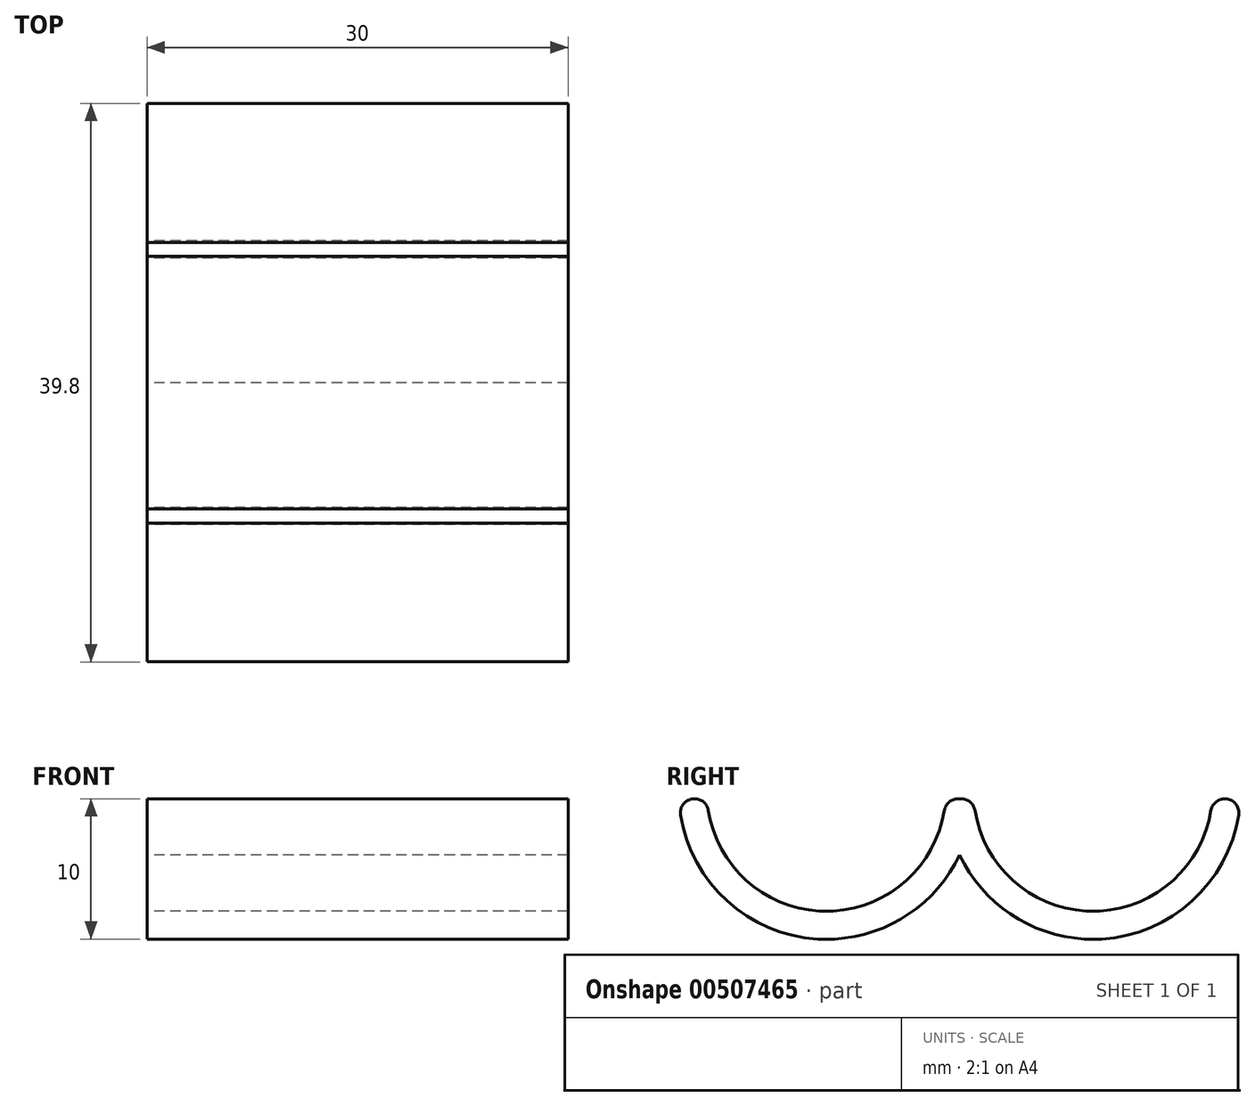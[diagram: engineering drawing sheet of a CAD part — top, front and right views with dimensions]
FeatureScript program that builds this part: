
annotation { "Feature Type Name" : "Feature", "Feature Type Description" : "" }
export const myFeature = defineFeature(function(context is Context, id is Id, definition is map)
    precondition{}
    {
        {
            var Q0;
            Q0=qCreatedBy(makeId("Right.planeOp"),FACE);
            var sketch = newSketch(context, id + "F0", { "sketchPlane" : qUnion([Q0])});
            skLineSegment(sketch, "E0", {"start": v(0, 0) * mm, "end": v(-1, 0) * mm});
            skLineSegment(sketch, "E1", {"start": v(-1, 0) * mm, "end": v(-1, 4) * mm});
            skLineSegment(sketch, "E2", {"start": v(-1, 8) * mm, "end": v(-2, 8) * mm});
            skPoint(sketch, "E3", {"position": v(-11, 0) * mm});
            skArc(sketch, "E4", {"start": v(-19, 8) * mm, "mid": v(-16.52, 2.48) * mm, "end": v(-11, 0) * mm});
            skLineSegment(sketch, "E5.MirrorCS", {"start": v(19, 8) * mm, "end": v(17, 8) * mm});
            skLineSegment(sketch, "E6.MirrorCS", {"start": v(-1, 8) * mm, "end": v(0, 8) * mm});
            skArc(sketch, "E7.MirrorCS", {"start": v(17, 8) * mm, "mid": v(14.52, 2.48) * mm, "end": v(9, 0) * mm});
            skPoint(sketch, "E8.MirrorP", {"position": v(9, 0) * mm});
            skArc(sketch, "E9.trimOffspring", {"start": v(-10, 0) * mm, "mid": v(-4.48, 2.48) * mm, "end": v(-2, 8) * mm});
            skArc(sketch, "E10.trimOffspring", {"start": v(8, 0) * mm, "mid": v(2.48, 2.48) * mm, "end": v(0, 8) * mm});
            skArc(sketch, "E11.0", {"start": v(-21, 7.88) * mm, "mid": v(-17.94, 1.06) * mm, "end": v(-11.12, -2) * mm});
            skArc(sketch, "E12.0", {"start": v(-9.88, -2) * mm, "mid": v(-4.62, -0.22) * mm, "end": v(-1, 4) * mm});
            skArc(sketch, "E13.0", {"start": v(7.88, -2) * mm, "mid": v(2.62, -0.22) * mm, "end": v(-1, 4) * mm});
            skArc(sketch, "E14.0", {"start": v(19, 7.88) * mm, "mid": v(15.94, 1.06) * mm, "end": v(9.12, -2) * mm});
            skLineSegment(sketch, "E15", {"start": v(-11.12, -2) * mm, "end": v(-9.88, -2) * mm});
            skLineSegment(sketch, "E16", {"start": v(7.88, -2) * mm, "end": v(9.12, -2) * mm});
            skLineSegment(sketch, "E17.trimOffspring", {"start": v(-10, 0) * mm, "end": v(-11, 0) * mm});
            skPoint(sketch, "E18.start.orphan", {"position": v(-22, 8) * mm});
            skLineSegment(sketch, "E19", {"start": v(-19, 8) * mm, "end": v(-21, 8) * mm});
            skLineSegment(sketch, "E20", {"start": v(-21, 7.88) * mm, "end": v(-21, 8) * mm});
            skPoint(sketch, "E21.end.orphan", {"position": v(-22, 0) * mm});
            skPoint(sketch, "E22.orphan", {"position": v(-19, 0) * mm});
            skLineSegment(sketch, "E23", {"start": v(19, 7.88) * mm, "end": v(19, 8) * mm});
            skPoint(sketch, "E24.MirrorCS.end.orphan", {"position": v(20, 8) * mm});
            skPoint(sketch, "E25.MirrorCS.end.orphan", {"position": v(20, 0) * mm});
            skPoint(sketch, "E26.orphan", {"position": v(17, 0) * mm});
            skLineSegment(sketch, "E27.trimOffspring", {"start": v(8, 0) * mm, "end": v(9, 0) * mm});
            skPoint(sketch, "E28.MirrorCS.start.orphan", {"position": v(-1, 0) * mm});
            skSolve(sketch);
        }
        {
            var Q0;
            Q0=makeQuery(id+"F0.imprint","IMPRINT",FACE,{"disambiguationData":[TD([[makeQuery(id+"F0.imprint","IMPRINT",EDGE,{"derivedFrom":sQuery(id+"F0.wireOp",EDGE,"E2")}),1.0]])]});
            extrude(context, id + "F1", {"entities" : qUnion([Q0]), "depth" : 30 * mm});
        }
        {
            var Q0;
            Q0=makeQuery(id+"F1.opExtrude","SWEPT_EDGE",EDGE,{"disambiguationData":[OSD([sQuery(id+"F0.wireOp",EDGE,"E4"),sQuery(id+"F0.wireOp",EDGE,"E19")])]});
            fillet(context, id + "F2", {"entities" : qUnion([Q0]), "radius" : 1 * mm, "tangentPropagation" : true, "allowEdgeOverflow" : false});
        }
        {
            var Q0;
            Q0=makeQuery(id+"F1.opExtrude","SWEPT_EDGE",EDGE,{"disambiguationData":[OSD([sQuery(id+"F0.wireOp",EDGE,"E19"),sQuery(id+"F0.wireOp",EDGE,"E20")])]});
            fillet(context, id + "F3", {"entities" : qUnion([Q0]), "radius" : 1 * mm, "tangentPropagation" : true, "allowEdgeOverflow" : false});
        }
        {
            var Q0;
            Q0=makeQuery(id+"F1.opExtrude","SWEPT_EDGE",EDGE,{"disambiguationData":[OSD([sQuery(id+"F0.wireOp",EDGE,"E2"),sQuery(id+"F0.wireOp",EDGE,"E9.trimOffspring")])]});
            var Q1;
            Q1=makeQuery(id+"F1.opExtrude","SWEPT_EDGE",EDGE,{"disambiguationData":[OSD([sQuery(id+"F0.wireOp",EDGE,"E6.MirrorCS"),sQuery(id+"F0.wireOp",EDGE,"E10.trimOffspring")])]});
            var Q2;
            Q2=makeQuery(id+"F1.opExtrude","SWEPT_EDGE",EDGE,{"disambiguationData":[OSD([sQuery(id+"F0.wireOp",EDGE,"E5.MirrorCS"),sQuery(id+"F0.wireOp",EDGE,"E23")])]});
            var Q3;
            Q3=makeQuery(id+"F1.opExtrude","SWEPT_EDGE",EDGE,{"disambiguationData":[OSD([sQuery(id+"F0.wireOp",EDGE,"E5.MirrorCS"),sQuery(id+"F0.wireOp",EDGE,"E7.MirrorCS")])]});
            fillet(context, id + "F4", {"entities" : qUnion([Q0, Q1, Q2, Q3]), "radius" : 1 * mm, "tangentPropagation" : true, "allowEdgeOverflow" : false});
        }
    });
